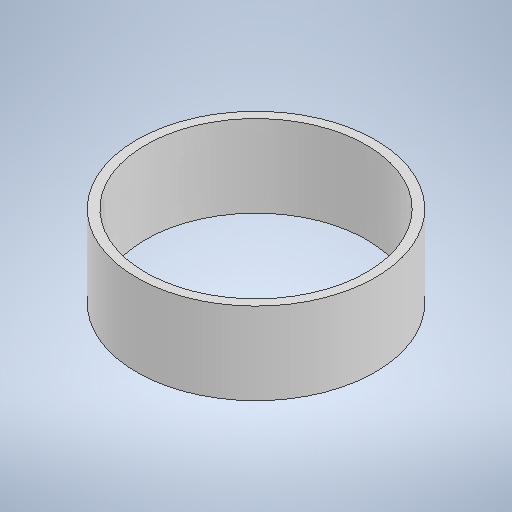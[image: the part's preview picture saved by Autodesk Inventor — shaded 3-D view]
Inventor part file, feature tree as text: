
AUTODESK INVENTOR PART (.ipt)
format: ipt  version: 2025.2 (Build 292293000, 293)  size: 265,728 bytes
history: native  units: mm
features: sketch x3, hole x2, extrude x1
ambient origin geometry x8: Origin, YZ Plane, XZ Plane, XY Plane, X Axis, Y Axis, Z Axis, Center Point
bodies: Solid1 (feature_tree)
feature tree (6):
  extrude  "Extrusion1"  Depth=67.0mm
  hole  "Hole1"  [1 undecoded]
  hole  "Hole2"  [1 undecoded]
  sketch  "Sketch1"  dims[d0=62.0mm d1=67.0mm]
  sketch  "Sketch3"  dims[d2=23.0mm d3=0.0mm]
  sketch  "Sketch4"  dims[d29=62.0mm d30=7.5mm d31=3.75mm d32=2.5mm d33=90.0deg d34=10.0mm d35=20.594885mm d39=62.0mm d40=7.5mm d41=3.75mm d42=2.5mm d43=90.0deg d44=10.0mm d45=20.594885mm]
note: 2 required parameter values undecoded (feature->parameter linkage not recoverable at this tier; creation-order binding heuristic only, values carry confidence <= 0.55)
